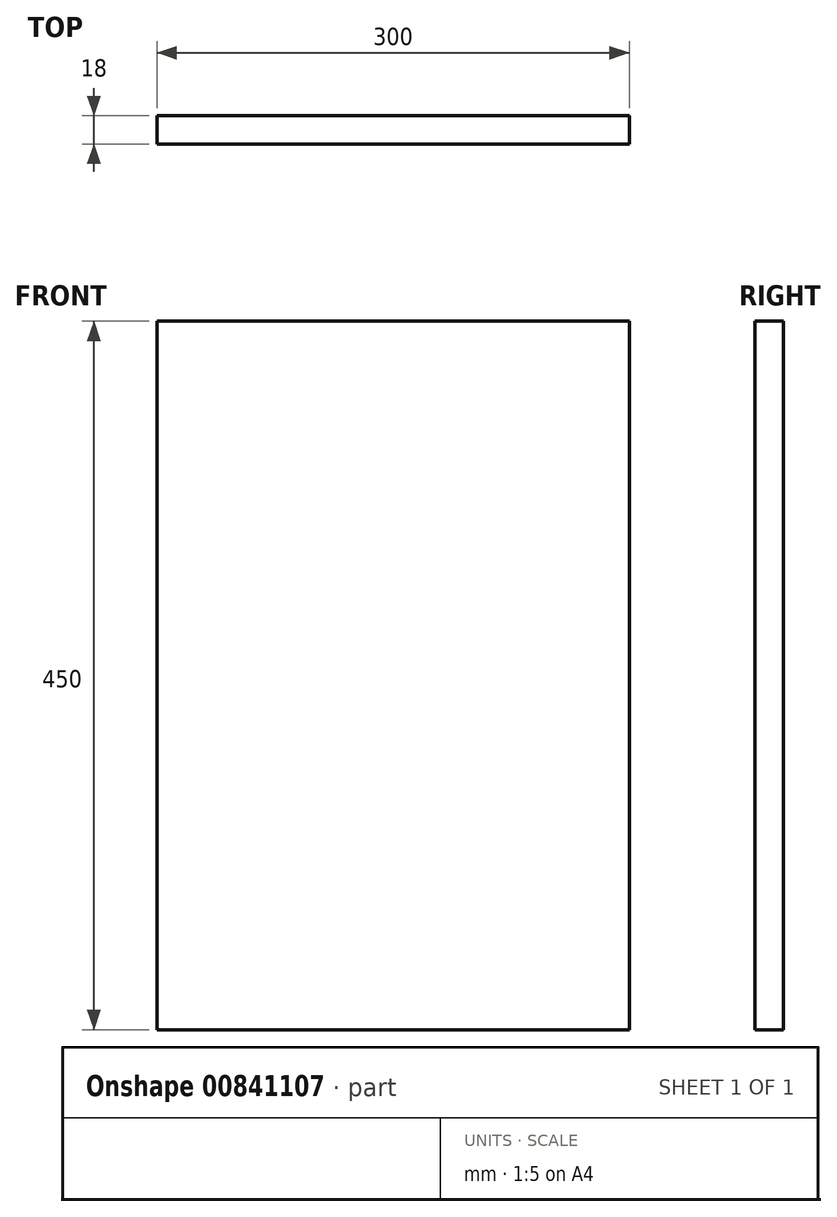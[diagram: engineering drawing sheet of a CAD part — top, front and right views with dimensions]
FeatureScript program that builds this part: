
annotation { "Feature Type Name" : "Feature", "Feature Type Description" : "" }
export const myFeature = defineFeature(function(context is Context, id is Id, definition is map)
    precondition{}
    {
        {
            var Q0;
            Q0=qCreatedBy(makeId("Top.planeOp"),FACE);
            var sketch = newSketch(context, id + "F0", { "sketchPlane" : qUnion([Q0])});
            skLineSegment(sketch, "E0.bottom", {"start": v(-150, -150) * mm, "end": v(150, -150) * mm});
            skLineSegment(sketch, "E0.top", {"start": v(-150, 150) * mm, "end": v(150, 150) * mm});
            skLineSegment(sketch, "E0.left", {"start": v(-150, -150) * mm, "end": v(-150, 150) * mm});
            skLineSegment(sketch, "E0.right", {"start": v(150, -150) * mm, "end": v(150, 150) * mm});
            skPoint(sketch, "E0.middle", {"position": v(0, 0) * mm});
            skSolve(sketch);
        }
        {
            var Q0;
            Q0=makeQuery(id+"F0.imprint","IMPRINT",FACE,{"disambiguationData":[TD([[makeQuery(id+"F0.imprint","IMPRINT",EDGE,{"derivedFrom":sQuery(id+"F0.wireOp",EDGE,"E0.bottom")}),1.0]])]});
            var Q1;
            Q1=sQuery(id+"F0.wireOp",EDGE,"E0.left");
            var Q2;
            Q2=sQuery(id+"F0.wireOp",EDGE,"E0.top");
            var Q3;
            Q3=sQuery(id+"F0.wireOp",EDGE,"E0.right");
            var Q4;
            Q4=sQuery(id+"F0.wireOp",EDGE,"E0.bottom");
            extrude(context, id + "F1", {"entities" : qUnion([Q0]), "bodyType" : ToolBodyType.SURFACE, "surfaceEntities" : qUnion([Q1, Q2, Q3, Q4]), "depth" : 450 * mm, "offsetDistance" : 25 * mm});
        }
        {
            var Q0;
            Q0=makeQuery(id+"F1.opExtrude","SWEPT_FACE",FACE,{"disambiguationData":[OSD([sQuery(id+"F0.wireOp",EDGE,"E0.top")])]});
            extrude(context, id + "F2", {"entities" : qUnion([Q0]), "depth" : 18 * mm, "offsetDistance" : 25 * mm});
        }
    });
